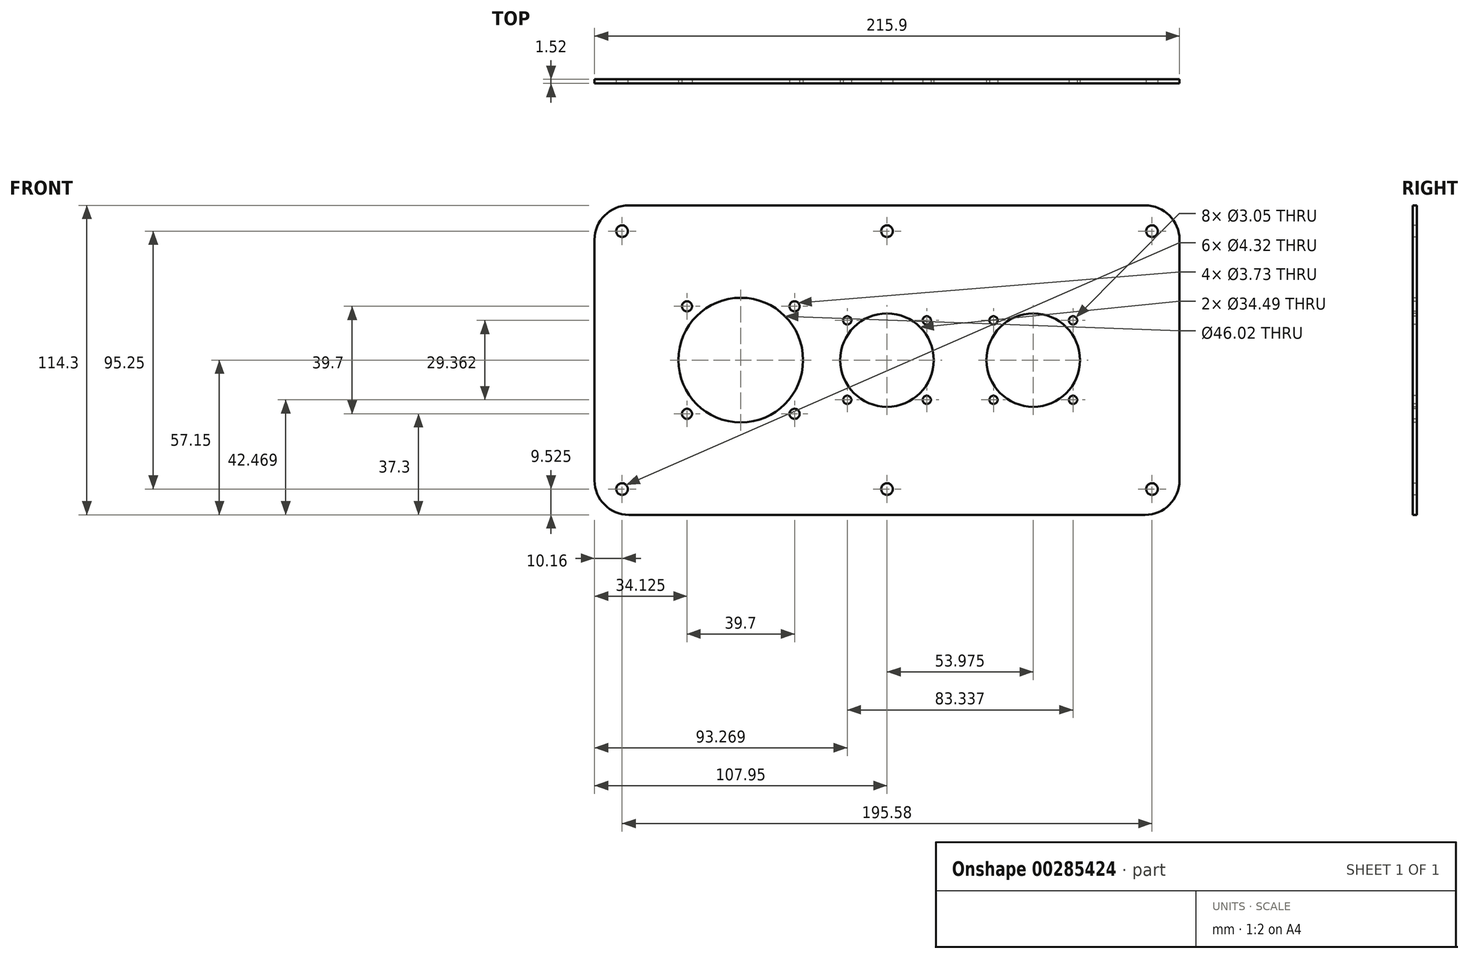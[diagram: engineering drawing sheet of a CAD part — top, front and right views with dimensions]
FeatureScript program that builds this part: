
annotation { "Feature Type Name" : "Feature", "Feature Type Description" : "" }
export const myFeature = defineFeature(function(context is Context, id is Id, definition is map)
    precondition{}
    {
        {
            var Q0;
            Q0=qCreatedBy(makeId("Front.planeOp"),FACE);
            var sketch = newSketch(context, id + "F0", { "sketchPlane" : qUnion([Q0])});
            skLineSegment(sketch, "E0.bottom", {"start": v(33.27, -22.23) * mm, "end": v(182.63, -22.23) * mm, "construction": true});
            skLineSegment(sketch, "E0.top", {"start": v(33.27, -92.08) * mm, "end": v(182.63, -92.08) * mm, "construction": true});
            skLineSegment(sketch, "E0.left", {"start": v(24.13, -31.37) * mm, "end": v(24.13, -82.93) * mm, "construction": true});
            skLineSegment(sketch, "E0.right", {"start": v(191.77, -31.37) * mm, "end": v(191.77, -82.93) * mm, "construction": true});
            skPoint(sketch, "E1.visualSharp", {"position": v(24.13, -22.23) * mm});
            skArc(sketch, "E1.filletArc", {"start": v(33.27, -22.23) * mm, "mid": v(26.8, -24.9) * mm, "end": v(24.13, -31.37) * mm, "construction": true});
            skPoint(sketch, "E2.visualSharp", {"position": v(191.77, -22.23) * mm});
            skArc(sketch, "E2.filletArc", {"start": v(191.77, -31.37) * mm, "mid": v(189.1, -24.9) * mm, "end": v(182.63, -22.22) * mm, "construction": true});
            skPoint(sketch, "E3.visualSharp", {"position": v(191.77, -92.08) * mm});
            skArc(sketch, "E3.filletArc", {"start": v(182.63, -92.08) * mm, "mid": v(189.1, -89.4) * mm, "end": v(191.77, -82.93) * mm, "construction": true});
            skPoint(sketch, "E4.visualSharp", {"position": v(24.13, -92.08) * mm});
            skArc(sketch, "E4.filletArc", {"start": v(24.13, -82.93) * mm, "mid": v(26.8, -89.4) * mm, "end": v(33.27, -92.07) * mm, "construction": true});
            skLineSegment(sketch, "E5.bottom", {"start": v(12.7, 0) * mm, "end": v(203.2, 0) * mm});
            skLineSegment(sketch, "E5.top", {"start": v(12.7, -114.3) * mm, "end": v(203.2, -114.3) * mm});
            skLineSegment(sketch, "E5.left", {"start": v(0, -12.7) * mm, "end": v(0, -101.6) * mm});
            skLineSegment(sketch, "E5.right", {"start": v(215.9, -12.7) * mm, "end": v(215.9, -101.6) * mm});
            skPoint(sketch, "E6.visualSharp", {"position": v(0, 0) * mm});
            skArc(sketch, "E6.filletArc", {"start": v(12.7, 0) * mm, "mid": v(3.72, -3.72) * mm, "end": v(0, -12.7) * mm});
            skPoint(sketch, "E7.visualSharp", {"position": v(215.9, 0) * mm});
            skArc(sketch, "E7.filletArc", {"start": v(215.9, -12.7) * mm, "mid": v(212.18, -3.72) * mm, "end": v(203.2, 0) * mm});
            skPoint(sketch, "E8.visualSharp", {"position": v(215.9, -114.3) * mm});
            skArc(sketch, "E8.filletArc", {"start": v(203.2, -114.3) * mm, "mid": v(212.18, -110.58) * mm, "end": v(215.9, -101.6) * mm});
            skPoint(sketch, "E9.visualSharp", {"position": v(0, -114.3) * mm});
            skArc(sketch, "E9.filletArc", {"start": v(0, -101.6) * mm, "mid": v(3.72, -110.58) * mm, "end": v(12.7, -114.3) * mm});
            skLineSegment(sketch, "E10", {"start": v(107.95, 0) * mm, "end": v(107.95, -114.3) * mm, "construction": true});
            skLineSegment(sketch, "E11", {"start": v(0, -57.15) * mm, "end": v(215.9, -57.15) * mm, "construction": true});
            skPoint(sketch, "E12", {"position": v(107.95, -22.23) * mm});
            skPoint(sketch, "E13", {"position": v(191.77, -57.15) * mm});
            skPoint(sketch, "E14", {"position": v(10.16, -9.52) * mm});
            skPoint(sketch, "E15", {"position": v(107.95, -9.52) * mm});
            skPoint(sketch, "E16", {"position": v(205.74, -9.52) * mm});
            skPoint(sketch, "E17", {"position": v(205.74, -104.78) * mm});
            skPoint(sketch, "E18", {"position": v(107.95, -104.78) * mm});
            skPoint(sketch, "E19", {"position": v(10.16, -104.78) * mm});
            skLineSegment(sketch, "E20", {"start": v(10.16, -9.52) * mm, "end": v(10.16, -104.78) * mm, "construction": true});
            skSolve(sketch);
        }
        {
            var Q0;
            Q0=makeQuery(id+"F0.imprint","IMPRINT",FACE,{"disambiguationData":[TD([[makeQuery(id+"F0.imprint","IMPRINT",EDGE,{"derivedFrom":sQuery(id+"F0.wireOp",EDGE,"E5.bottom")}),-1.0]])]});
            extrude(context, id + "F1", {"entities" : qUnion([Q0]), "depth" : 1.52 * mm});
        }
        {
            var Q0;
            Q0=makeQuery(id+"F1.opExtrude","CAP_FACE",FACE,{"disambiguationData":[OSD([sQuery(id+"F0.wireOp",EDGE,"E5.bottom"),sQuery(id+"F0.wireOp",EDGE,"E5.top"),sQuery(id+"F0.wireOp",EDGE,"E5.left"),sQuery(id+"F0.wireOp",EDGE,"E5.right"),sQuery(id+"F0.wireOp",EDGE,"E6.filletArc"),sQuery(id+"F0.wireOp",EDGE,"E7.filletArc"),sQuery(id+"F0.wireOp",EDGE,"E8.filletArc"),sQuery(id+"F0.wireOp",EDGE,"E9.filletArc")])],"isStart":false});
            var sketch = newSketch(context, id + "F2", { "sketchPlane" : qUnion([Q0])});
            skCircle(sketch, "E21", {"center": v(53.97, -57.15) * mm, "radius": 23.01 * mm});
            skCircle(sketch, "E22", {"center": v(34.12, -37.3) * mm, "radius": 1.87 * mm});
            skLineSegment(sketch, "E23.bottom", {"start": v(34.12, -37.3) * mm, "end": v(73.83, -37.3) * mm, "construction": true});
            skLineSegment(sketch, "E23.top", {"start": v(34.12, -77) * mm, "end": v(73.83, -77) * mm, "construction": true});
            skLineSegment(sketch, "E23.left", {"start": v(34.12, -37.3) * mm, "end": v(34.12, -77) * mm, "construction": true});
            skLineSegment(sketch, "E23.right", {"start": v(73.83, -37.3) * mm, "end": v(73.83, -77) * mm, "construction": true});
            skLineSegment(sketch, "E24", {"start": v(53.98, -37.3) * mm, "end": v(53.98, -77) * mm, "construction": true});
            skLineSegment(sketch, "E25", {"start": v(34.12, -57.15) * mm, "end": v(73.83, -57.15) * mm, "construction": true});
            skCircle(sketch, "E26", {"center": v(73.83, -37.3) * mm, "radius": 1.87 * mm});
            skCircle(sketch, "E27", {"center": v(73.83, -77) * mm, "radius": 1.87 * mm});
            skCircle(sketch, "E28", {"center": v(34.12, -77) * mm, "radius": 1.87 * mm});
            skCircle(sketch, "E29", {"center": v(161.93, -57.15) * mm, "radius": 17.25 * mm});
            skCircle(sketch, "E30", {"center": v(147.24, -42.47) * mm, "radius": 1.52 * mm});
            skLineSegment(sketch, "E31.bottom", {"start": v(147.24, -42.47) * mm, "end": v(176.6, -42.47) * mm, "construction": true});
            skLineSegment(sketch, "E31.top", {"start": v(147.24, -71.83) * mm, "end": v(176.6, -71.83) * mm, "construction": true});
            skLineSegment(sketch, "E31.left", {"start": v(147.24, -42.47) * mm, "end": v(147.24, -71.83) * mm, "construction": true});
            skLineSegment(sketch, "E31.right", {"start": v(176.6, -42.47) * mm, "end": v(176.6, -71.83) * mm, "construction": true});
            skLineSegment(sketch, "E32", {"start": v(161.93, -42.47) * mm, "end": v(161.93, -71.83) * mm, "construction": true});
            skLineSegment(sketch, "E33", {"start": v(147.24, -57.15) * mm, "end": v(176.6, -57.15) * mm, "construction": true});
            skCircle(sketch, "E34", {"center": v(176.6, -42.47) * mm, "radius": 1.52 * mm});
            skCircle(sketch, "E35", {"center": v(176.6, -71.83) * mm, "radius": 1.52 * mm});
            skCircle(sketch, "E36", {"center": v(147.24, -71.83) * mm, "radius": 1.52 * mm});
            skCircle(sketch, "E37", {"center": v(107.95, -57.15) * mm, "radius": 17.25 * mm});
            skLineSegment(sketch, "E38.bottom", {"start": v(93.27, -42.47) * mm, "end": v(122.63, -42.47) * mm, "construction": true});
            skLineSegment(sketch, "E38.top", {"start": v(93.27, -71.83) * mm, "end": v(122.63, -71.83) * mm, "construction": true});
            skLineSegment(sketch, "E38.left", {"start": v(93.27, -42.47) * mm, "end": v(93.27, -71.83) * mm, "construction": true});
            skLineSegment(sketch, "E38.right", {"start": v(122.63, -42.47) * mm, "end": v(122.63, -71.83) * mm, "construction": true});
            skLineSegment(sketch, "E39", {"start": v(122.63, -57.15) * mm, "end": v(93.27, -57.15) * mm, "construction": true});
            skLineSegment(sketch, "E40", {"start": v(107.95, -71.83) * mm, "end": v(107.95, -42.47) * mm, "construction": true});
            skCircle(sketch, "E41", {"center": v(93.27, -42.47) * mm, "radius": 1.52 * mm});
            skCircle(sketch, "E42", {"center": v(122.63, -42.47) * mm, "radius": 1.52 * mm});
            skCircle(sketch, "E43", {"center": v(122.63, -71.83) * mm, "radius": 1.52 * mm});
            skCircle(sketch, "E44", {"center": v(93.27, -71.83) * mm, "radius": 1.52 * mm});
            skSolve(sketch);
        }
        {
            var Q0;
            Q0 = qSketchRegion(id + "F2", true);
            extrude(context, id + "F3", {"entities" : qUnion([Q0]), "operationType" : NewBodyOperationType.REMOVE, "endBound" : BoundingType.THROUGH_ALL, "oppositeDirection" : true, "depth" : 25.4 * mm});
        }
        {
            var Q0;
            {var subQ23=sQuery(id+"F0.wireOp",EDGE,"E9.filletArc");var subQ26=sQuery(id+"F0.wireOp",EDGE,"E8.filletArc");var subQ29=sQuery(id+"F0.wireOp",EDGE,"E7.filletArc");var subQ32=sQuery(id+"F0.wireOp",EDGE,"E6.filletArc");var subQ35=sQuery(id+"F0.wireOp",EDGE,"E5.left");var subQ107=sQuery(id+"F0.wireOp",EDGE,"E5.bottom");var subQ108=makeQuery(id+"F1.opExtrude","SWEPT_FACE",FACE,{"disambiguationData":[OSD([subQ107])]});var subQ120=sQuery(id+"F0.wireOp",EDGE,"E5.right");var subQ124=sQuery(id+"F0.wireOp",EDGE,"E5.top");Q0=makeQuery(id+"F0iIbDMZRCul3dS_1.boolean.opBoolean","SPLIT",FACE,{"disambiguationData":[TD([subQ108])],"derivedFrom":makeQuery(id+"FoBDLu0VgXb6mYX_1.boolean.opBoolean","SPLIT",FACE,{"disambiguationData":[TD([subQ108])],"derivedFrom":makeQuery(id+"F1.opExtrude","CAP_FACE",FACE,{"disambiguationData":[OSD([subQ107,subQ124,subQ35,subQ120,subQ32,subQ29,subQ26,subQ23])],"isStart":false})})});}
            var sketch = newSketch(context, id + "F4", { "sketchPlane" : qUnion([Q0])});
            skPoint(sketch, "E45", {"position": v(10.16, -9.52) * mm});
            skPoint(sketch, "E46", {"position": v(107.95, -9.52) * mm});
            skPoint(sketch, "E47", {"position": v(205.74, -9.52) * mm});
            skPoint(sketch, "E48", {"position": v(205.74, -104.78) * mm});
            skPoint(sketch, "E49", {"position": v(107.95, -104.78) * mm});
            skPoint(sketch, "E50", {"position": v(10.16, -104.78) * mm});
            skSolve(sketch);
        }
        {
            var Q0;
            Q0=sQuery(id+"F4.wireOp",VERTEX,"E45");
            var Q1;
            Q1=sQuery(id+"F4.wireOp",VERTEX,"E46");
            var Q2;
            Q2=sQuery(id+"F4.wireOp",VERTEX,"E47");
            var Q3;
            Q3=sQuery(id+"F4.wireOp",VERTEX,"E48");
            var Q4;
            Q4=sQuery(id+"F4.wireOp",VERTEX,"E49");
            var Q5;
            Q5=sQuery(id+"F4.wireOp",VERTEX,"E50");
            var Q6;
            Q6=makeQuery(id+"F1.opExtrude","SWEPT_BODY",BODY,{"disambiguationData":[OSD([sQuery(id+"F0.wireOp",EDGE,"E5.bottom"),sQuery(id+"F0.wireOp",EDGE,"E5.top"),sQuery(id+"F0.wireOp",EDGE,"E5.left"),sQuery(id+"F0.wireOp",EDGE,"E5.right"),sQuery(id+"F0.wireOp",EDGE,"E6.filletArc"),sQuery(id+"F0.wireOp",EDGE,"E7.filletArc"),sQuery(id+"F0.wireOp",EDGE,"E8.filletArc"),sQuery(id+"F0.wireOp",EDGE,"E9.filletArc")])]});
            hole(context, id + "F5", {"style" : HoleStyle.SIMPLE, "endStyle" : HoleEndStyle.THROUGH, "standardTappedOrClearance" : lookupTablePath({ "standard" : "ANSI", "fit" : "Close", "size" : "#8", "type" : "Clearance" }), "standardBlindInLast" : lookupTablePath({ "fit" : "Close", "standard" : "ANSI", "size" : "#8", "type" : "Clearance" }), "holeDiameter" : 4.32 * mm, "isTappedThrough" : true, "tappedDepth" : 2.4 * mm, "tapClearance" : 3, "startFromSketch" : true, "locations" : qUnion([Q0, Q1, Q2, Q3, Q4, Q5]), "scope" : qUnion([Q6])});
        }
    });
